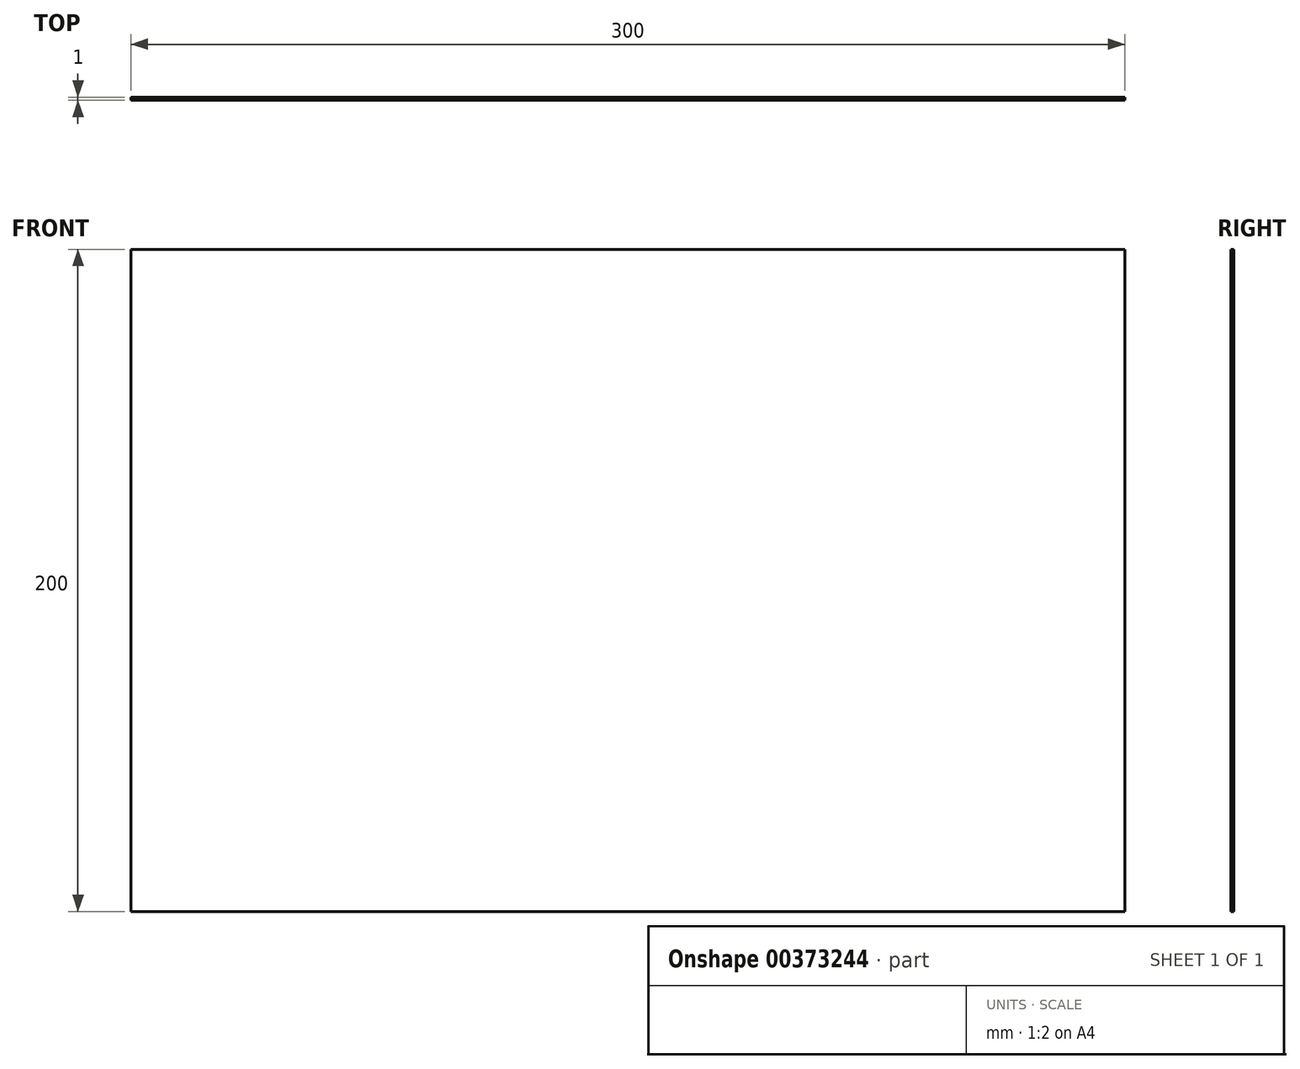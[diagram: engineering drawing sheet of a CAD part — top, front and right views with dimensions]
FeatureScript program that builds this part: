
annotation { "Feature Type Name" : "Feature", "Feature Type Description" : "" }
export const myFeature = defineFeature(function(context is Context, id is Id, definition is map)
    precondition{}
    {
        {
            var Q0;
            Q0=qCreatedBy(makeId("Front.planeOp"),FACE);
            var sketch = newSketch(context, id + "F0", { "sketchPlane" : qUnion([Q0])});
            skLineSegment(sketch, "E0.bottom", {"start": v(-67.48, 164.67) * mm, "end": v(232.52, 164.67) * mm});
            skLineSegment(sketch, "E0.top", {"start": v(-67.48, -35.33) * mm, "end": v(232.52, -35.33) * mm});
            skLineSegment(sketch, "E0.left", {"start": v(-67.48, 164.67) * mm, "end": v(-67.48, -35.33) * mm});
            skLineSegment(sketch, "E0.right", {"start": v(232.52, 164.67) * mm, "end": v(232.52, -35.33) * mm});
            skSolve(sketch);
        }
        {
            var Q0;
            Q0=qSketchRegion(id+"F0",true);
            extrude(context, id + "F1", {"entities" : qUnion([Q0]), "depth" : 1 * mm});
        }
    });
